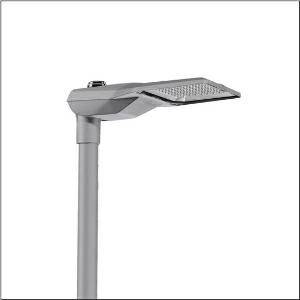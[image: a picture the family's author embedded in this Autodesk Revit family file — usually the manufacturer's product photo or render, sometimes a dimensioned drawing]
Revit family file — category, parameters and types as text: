
# Revit family: streetlight_sl_21_midi___st1_0a_5xe7d27n08mb_7be8
name_source: partatom
category: Lighting Fixtures
units: mm (PartAtom-declared; Revit-internal decimal feet)

## family parameters
Cut with Voids When Loaded = No
Host = Face
Light Source = No
Part Type = Normal
Room Calculation Point = No
Round Connector Dimension = Use Diameter
Shared = No

## types (1)
- --- (1 x LED, 14990 lm, 134.3 W, 2200K)
    Apparent Load = 134 VA
    CIE Flux Codes = 37 72 97 100 100
    Color Rendering = 70
    Color Temperature = 2200K
    Default Elevation = 1800 mm
    Description = Streetlight SL 21 midi, mast luminaire, primary light control with lens, of PMMA, primary optical cover: cover, of toughened safety glass, transparent, light distribution: ST1.0a, light emission: direct distribution, primary light characteristic: asymmetric, installation type: side-entry, LED, 3G 2.5mm², High Power LED, rated luminous flux: 14.990lm, luminous efficacy: 112lm/W, light colour: 722, colour temperature: 2200K, control gear: NEMA (7pin), control: overheat protection, pre-setting: linear dimming characteristic, constant luminous flux control, time-dependent luminous flux control, flexible luminous flux parameterisation, mains connection: 220..240V, AC, 50/60Hz, connection cable pre-assembled, cable length: 12,5m, wiring characteristics: H05VV-F, start of lifetime: 134W, end of service life: 141W, reduction: 60W, luminaire housing, of diecast aluminium (EN AC-44300), powder-coated, SITECO metallic grey (DB 702S), corrosivity category C5 high according to DIN EN ISO 12944, multi-level sealing system, sealing non-destructively replaceable, inclination adjustable: 0°, 5°, 10°, 15°, length: 644mm, width: 335mm, height: 110mm, spigot size: 42mm (side-entry), mounting height: 4..8m, protection rating (complete): IP66, insulation class (complete): insulation class I (protective earthing), certification: CE, ENEC, ENEC+, VDE, impact resistance: IK10, permissible operating ambient temperature for outdoor applications: -40..+50°C, standard-compliant lighting for roads and squares, packaging unit: 1 piece

Light Distribution: ST1.0a
    Height = 111 mm
    Lamp = 1 x LED
    Lamp Light Flux = 14990 lm
    Lamp Power = 134.3 W
    Lamp count = 1
    Length = 644 mm
    Luminous efficacy = 112 lm/W
    Manufacturer = Siteco
    ModVariant = No
    Model = 5XE7D27N08MB
    Mounting Place = Pole
    Mounting Type = Pole top
    Number of Poles = 1
    OnlyDefault = Yes
    Power Factor = 1
    Product Name = Streetlight SL 21 midi | ST1.0a
    Product group = mast luminaire | pylon top
    ProductGroupID = 6100
    Protection Class = Protection class I
    Protection Degree = IP 66
    RLX_Detail_Level = 1
    RLX_Emergency_Light_Flux = 0 lm
    RLX_Emergency_Type = 0
    RLX_Emergency_Type_DB = No
    RlxData = <blob elided: 26465 chars, md5=a5580b00>
    Socket = socket
    Standby Power = 0 W
    System Light Flux = 14991 lm
    System Power = 134 W
    Type Comments = factory setting: luminous flux: 100 % | dim-lin: 254 | 687 mA
    Type Image = l_1294377.jpg
    URL = http://relux.com
    VarID = @adj_137177
    Voltage = 0 V
    Weight = 0.00 kg
    Width = 336 mm

## geometry (parser evidence)
native form markers: Blend x4, Sweep x10
no freeform markers — native parametric forms only
